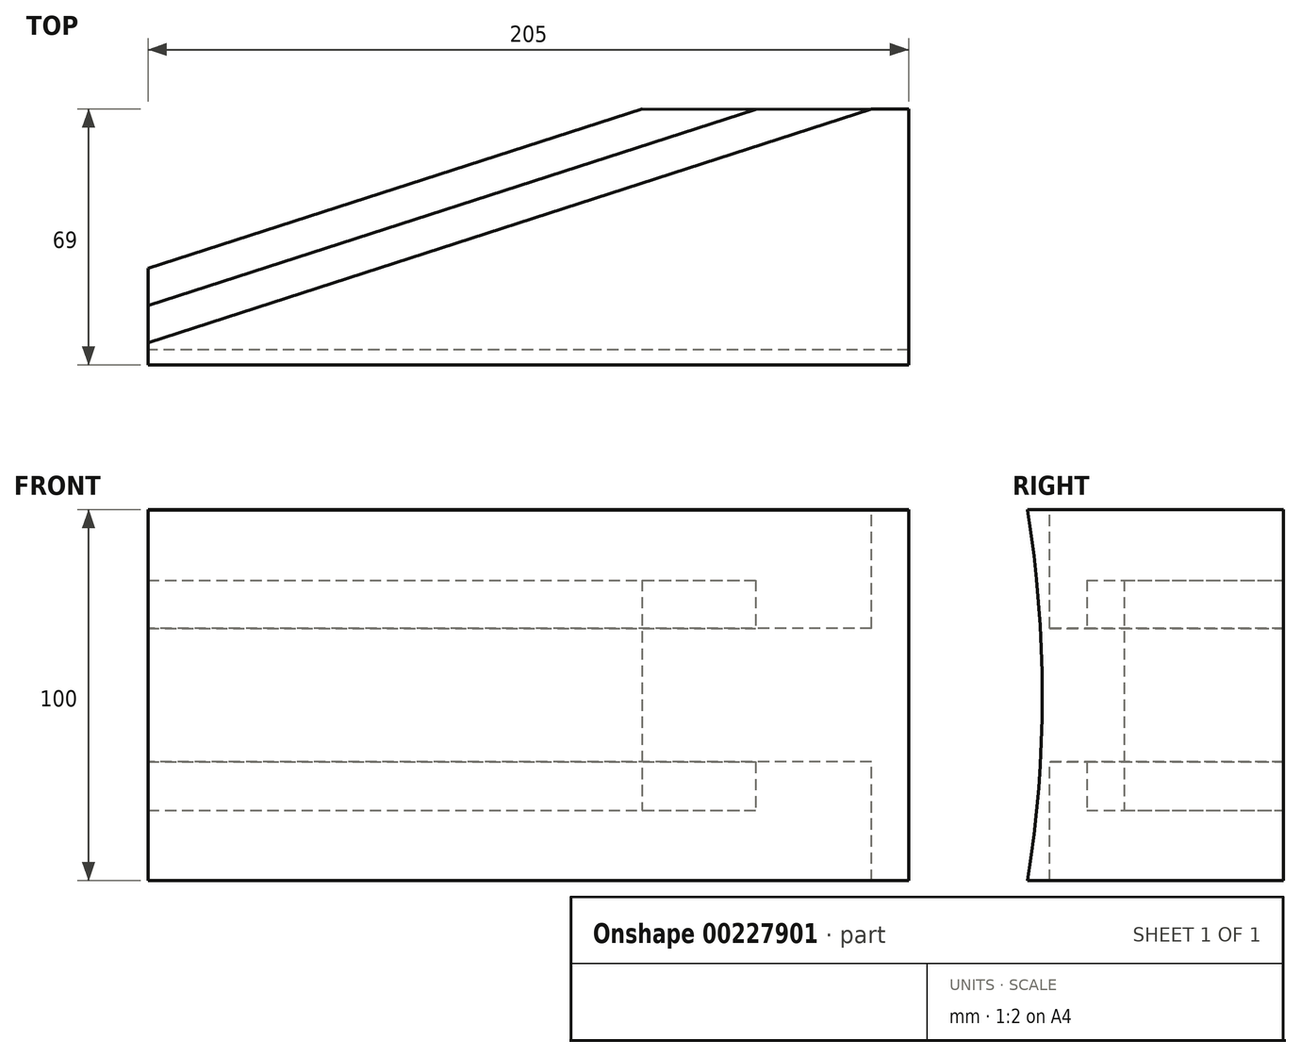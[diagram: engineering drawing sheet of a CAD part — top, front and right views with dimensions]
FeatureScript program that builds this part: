
annotation { "Feature Type Name" : "Feature", "Feature Type Description" : "" }
export const myFeature = defineFeature(function(context is Context, id is Id, definition is map)
    precondition{}
    {
        {
            var Q0;
            Q0=qCreatedBy(makeId("Top.planeOp"),FACE);
            var sketch = newSketch(context, id + "F0", { "sketchPlane" : qUnion([Q0])});
            skLineSegment(sketch, "E0", {"start": v(0, 0) * mm, "end": v(205, 0) * mm});
            skLineSegment(sketch, "E1", {"start": v(0, 0) * mm, "end": v(0, 6) * mm});
            skLineSegment(sketch, "E2", {"start": v(0, 6) * mm, "end": v(0, 16) * mm});
            skLineSegment(sketch, "E3", {"start": v(0, 16) * mm, "end": v(0, 26) * mm});
            skLineSegment(sketch, "E4", {"start": v(205, 0) * mm, "end": v(205, 69) * mm});
            skLineSegment(sketch, "E5", {"start": v(205, 69) * mm, "end": v(195, 69) * mm});
            skLineSegment(sketch, "E6", {"start": v(195, 69) * mm, "end": v(0, 6) * mm});
            skLineSegment(sketch, "E7", {"start": v(0, 16) * mm, "end": v(163.7, 68.89) * mm});
            skLineSegment(sketch, "E8", {"start": v(0, 26) * mm, "end": v(133.1, 69) * mm});
            skLineSegment(sketch, "E9", {"start": v(195, 69) * mm, "end": v(163.7, 68.89) * mm});
            skLineSegment(sketch, "E10", {"start": v(133.1, 69) * mm, "end": v(163.7, 68.89) * mm});
            skSolve(sketch);
        }
        {
            var Q0;
            Q0=makeQuery(id+"F0.imprint","IMPRINT",FACE,{"disambiguationData":[TD([[makeQuery(id+"F0.imprint","IMPRINT",EDGE,{"derivedFrom":sQuery(id+"F0.wireOp",EDGE,"E0")}),1.0]])]});
            extrude(context, id + "F1", {"entities" : qUnion([Q0]), "oppositeDirection" : true, "depth" : 50 * mm});
        }
        {
            var Q0;
            Q0=makeQuery(id+"F0.imprint","IMPRINT",FACE,{"disambiguationData":[TD([[makeQuery(id+"F0.imprint","IMPRINT",EDGE,{"derivedFrom":sQuery(id+"F0.wireOp",EDGE,"E0")}),1.0]])]});
            extrude(context, id + "F2", {"entities" : qUnion([Q0]), "operationType" : NewBodyOperationType.ADD, "depth" : 50 * mm});
        }
        {
            var Q0;
            Q0=makeQuery(id+"F0.imprint","IMPRINT",FACE,{"disambiguationData":[TD([[makeQuery(id+"F0.imprint","IMPRINT",EDGE,{"derivedFrom":sQuery(id+"F0.wireOp",EDGE,"E2")}),-1.0]])]});
            extrude(context, id + "F3", {"entities" : qUnion([Q0]), "operationType" : NewBodyOperationType.ADD, "depth" : 18 * mm});
        }
        {
            var Q0;
            Q0=makeQuery(id+"F3.opExtrude","CAP_FACE",FACE,{"disambiguationData":[OSD([sQuery(id+"F0.wireOp",EDGE,"E2"),sQuery(id+"F0.wireOp",EDGE,"E6"),sQuery(id+"F0.wireOp",EDGE,"E7"),sQuery(id+"F0.wireOp",EDGE,"E9")])],"isStart":true});
            extrude(context, id + "F4", {"entities" : qUnion([Q0]), "operationType" : NewBodyOperationType.ADD, "depth" : 18 * mm});
        }
        {
            var Q0;
            Q0=makeQuery(id+"F0.imprint","IMPRINT",FACE,{"disambiguationData":[TD([[makeQuery(id+"F0.imprint","IMPRINT",EDGE,{"derivedFrom":sQuery(id+"F0.wireOp",EDGE,"E3")}),-1.0]])]});
            extrude(context, id + "F5", {"entities" : qUnion([Q0]), "operationType" : NewBodyOperationType.ADD, "endBound" : BoundingType.SYMMETRIC, "depth" : 62 * mm});
        }
        {
            var Q0;
            Q0=qCreatedBy(makeId("Right.planeOp"),FACE);
            var sketch = newSketch(context, id + "F6", { "sketchPlane" : qUnion([Q0])});
            skArc(sketch, "E11", {"start": v(0, -50.24) * mm, "mid": v(4, -0.16) * mm, "end": v(0, 49.93) * mm});
            skLineSegment(sketch, "E12", {"start": v(0, -50.24) * mm, "end": v(0, 49.93) * mm});
            skSolve(sketch);
        }
        {
            var Q0;
            Q0=makeQuery(id+"F6.imprint","IMPRINT",FACE,{"disambiguationData":[TD([[makeQuery(id+"F6.imprint","IMPRINT",EDGE,{"derivedFrom":sQuery(id+"F6.wireOp",EDGE,"E11")}),1.0]])]});
            extrude(context, id + "F7", {"entities" : qUnion([Q0]), "operationType" : NewBodyOperationType.REMOVE, "endBound" : BoundingType.THROUGH_ALL, "depth" : 25 * mm});
        }
    });
